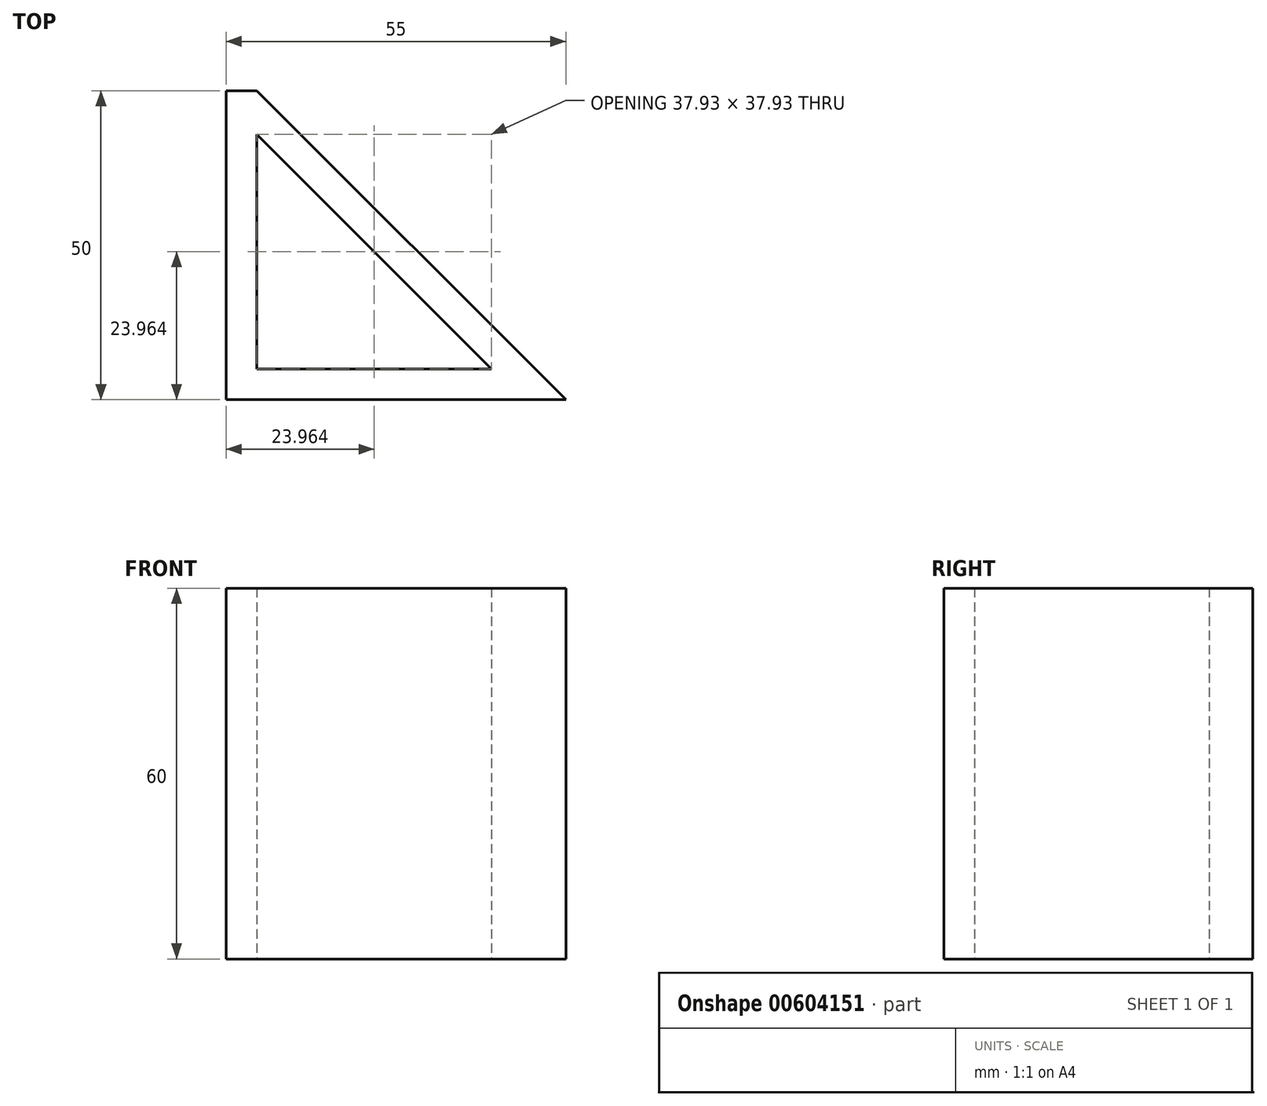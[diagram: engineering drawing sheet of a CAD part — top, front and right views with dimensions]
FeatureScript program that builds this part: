
annotation { "Feature Type Name" : "Feature", "Feature Type Description" : "" }
export const myFeature = defineFeature(function(context is Context, id is Id, definition is map)
    precondition{}
    {
        {
            var Q0;
            Q0=qCreatedBy(makeId("Top.planeOp"),FACE);
            var sketch = newSketch(context, id + "F0", { "sketchPlane" : qUnion([Q0])});
            skLineSegment(sketch, "E0", {"start": v(0, 0) * mm, "end": v(-55, 0) * mm});
            skLineSegment(sketch, "E1", {"start": v(-55, 0) * mm, "end": v(-55, 50) * mm});
            skLineSegment(sketch, "E2", {"start": v(-55, 50) * mm, "end": v(-50, 50) * mm});
            skLineSegment(sketch, "E3", {"start": v(-50, 50) * mm, "end": v(0, 0) * mm});
            skLineSegment(sketch, "E4.0", {"start": v(-50, 42.93) * mm, "end": v(-12.07, 5) * mm});
            skLineSegment(sketch, "E4.1", {"start": v(-50, 5) * mm, "end": v(-50, 42.93) * mm});
            skLineSegment(sketch, "E4.2", {"start": v(-12.07, 5) * mm, "end": v(-50, 5) * mm});
            skSolve(sketch);
        }
        {
            var Q0;
            Q0=makeQuery(id+"F0.imprint","IMPRINT",FACE,{"disambiguationData":[TD([[makeQuery(id+"F0.imprint","IMPRINT",EDGE,{"derivedFrom":sQuery(id+"F0.wireOp",EDGE,"E0")}),-1.0]])]});
            extrude(context, id + "F1", {"entities" : qUnion([Q0]), "depth" : 60 * mm, "offsetDistance" : 25 * mm});
        }
    });
